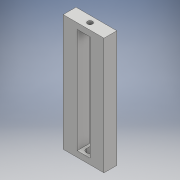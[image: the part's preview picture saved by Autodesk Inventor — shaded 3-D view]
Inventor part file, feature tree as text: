
AUTODESK INVENTOR PART (.ipt)
format: ipt  version: 2017 (Build 210142000, 142)  size: 179,712 bytes
history: native  units: mm
features: extrude x7, sketch x5, projected_geometry x1
ambient origin geometry x8: Origin, YZ Plane, XZ Plane, XY Plane, X Axis, Y Axis, Z Axis, Center Point
bodies: Solid1 (feature_tree)
feature tree (13):
  sketch  "Sketch1"  dims[d0=6.2mm d1=11.0mm]
  extrude  "Extr-legs"  Depth=11.0mm
  extrude  "Extr-base"  Depth=12.0mm
  sketch  "Sketch2"  dims[d2=12.0mm d3=12.0mm]
  extrude  "Extr-top"  Depth=5.0mm TaperAngle=0.0deg
  extrude  "Extrusion4"  Depth=9.0mm
  extrude  "Extrusion5"  Depth=10.0mm TaperAngle=0.0deg
  extrude  "Extrusion6"  Depth=10.0mm TaperAngle=0.0deg
  extrude  "Extrusion7"  Depth=10.0mm TaperAngle=0.0deg
  sketch  "Sketch3"  dims[d4=90.0mm d5=0.0mm d6=5.0mm d7=0.0mm]
  projected_geometry  "Projected Loop1"
  sketch  "Sketch4"  dims[d8=4.4mm d9=9.0mm]
  sketch  "Sketch5"  dims[d10=5.0mm d11=0.0mm d12=10.0mm d13=0.0mm d15=10.0mm d16=0.0mm d17=10.0mm d18=0.0mm d19=10.0mm d20=0.0mm]
